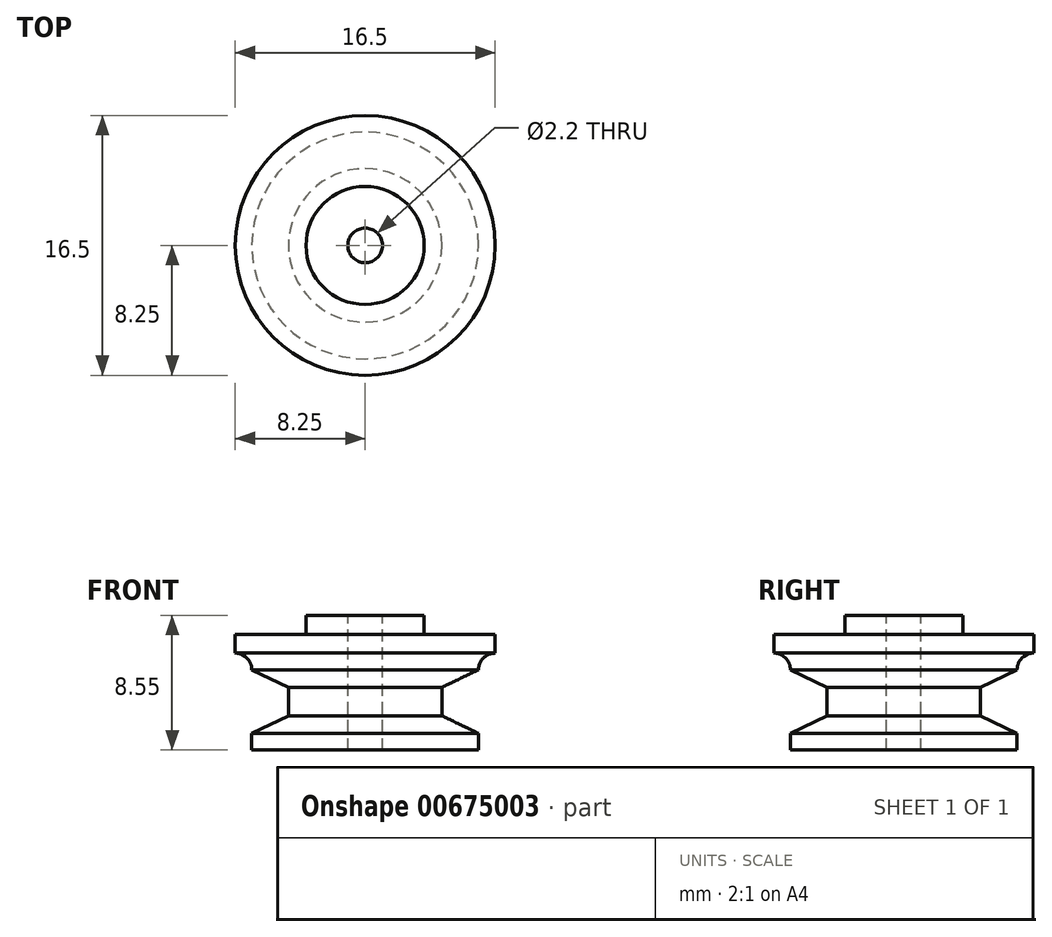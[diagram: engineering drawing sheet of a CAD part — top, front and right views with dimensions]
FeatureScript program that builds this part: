
annotation { "Feature Type Name" : "Feature", "Feature Type Description" : "" }
export const myFeature = defineFeature(function(context is Context, id is Id, definition is map)
    precondition{}
    {
        {
            assignVariable(context, id + "F0", {"name" : "Faktor", "anyValue" : 1.5});
        }
        {
            var Q0;
            Q0=qCreatedBy(makeId("Front.planeOp"),FACE);
            var sketch = newSketch(context, id + "F1", { "sketchPlane" : qUnion([Q0])});
            skLineSegment(sketch, "E0", {"start": v(0, 0) * mm, "end": v(-7.2, 0) * mm});
            skLineSegment(sketch, "E1", {"start": v(-7.2, 0) * mm, "end": v(-7.2, 1.05) * mm});
            skLineSegment(sketch, "E2", {"start": v(-7.2, 1.05) * mm, "end": v(-4.87, 2.18) * mm});
            skLineSegment(sketch, "E3", {"start": v(-4.88, 2.18) * mm, "end": v(-4.88, 3.98) * mm});
            skLineSegment(sketch, "E4", {"start": v(-4.87, 3.98) * mm, "end": v(-7.2, 5.1) * mm});
            skLineSegment(sketch, "E5", {"start": v(-7.2, 5.1) * mm, "end": v(-7.2, 6.15) * mm});
            skLineSegment(sketch, "E6", {"start": v(-7.2, 6.15) * mm, "end": v(-8.25, 6.15) * mm});
            skLineSegment(sketch, "E7", {"start": v(-8.25, 6.15) * mm, "end": v(-8.25, 7.35) * mm});
            skLineSegment(sketch, "E8", {"start": v(-8.25, 7.35) * mm, "end": v(-3.75, 7.35) * mm});
            skLineSegment(sketch, "E9", {"start": v(-3.75, 7.35) * mm, "end": v(-3.75, 8.55) * mm});
            skLineSegment(sketch, "E10", {"start": v(-3.75, 8.55) * mm, "end": v(0, 8.55) * mm});
            skLineSegment(sketch, "E11", {"start": v(0, 8.55) * mm, "end": v(0, 0) * mm});
            skLineSegment(sketch, "E12", {"start": v(-11.17, 3.08) * mm, "end": v(3.9, 3.08) * mm, "construction": true});
            skSolve(sketch);
        }
        {
            var Q0;
            Q0=qSketchRegion(id+"F1",true);
            var Q1;
            Q1=sQuery(id+"F1.wireOp",EDGE,"E11");
            revolve(context, id + "F2", {"entities" : qUnion([Q0]), "axis" : qUnion([Q1]), "revolveType" : RevolveType.FULL});
        }
        {
            var Q0;
            Q0=makeQuery(id+"F2.opRevolve","SWEPT_EDGE",EDGE,{"disambiguationData":[OSD([sQuery(id+"F1.wireOp",EDGE,"E5"),sQuery(id+"F1.wireOp",EDGE,"E6")])]});
            fillet(context, id + "F3", {"entities" : qUnion([Q0]), "radius" : getVariable(context, 'Faktor') * 0.7 * mm, "tangentPropagation" : true, "allowEdgeOverflow" : false});
        }
        {
            var Q0;
            Q0=makeQuery(id+"F2.opRevolve","SWEPT_FACE",FACE,{"disambiguationData":[OSD([sQuery(id+"F1.wireOp",EDGE,"E10")])]});
            var sketch = newSketch(context, id + "F4", { "sketchPlane" : qUnion([Q0])});
            skCircle(sketch, "E13", {"center": v(0, 0) * mm, "radius": 1.1 * mm});
            skSolve(sketch);
        }
        {
            var Q0;
            Q0=qSketchRegion(id+"F4",true);
            extrude(context, id + "F5", {"entities" : qUnion([Q0]), "operationType" : NewBodyOperationType.REMOVE, "endBound" : BoundingType.THROUGH_ALL, "oppositeDirection" : true, "depth" : 0.8 * mm, "offsetDistance" : 25 * mm});
        }
    });
